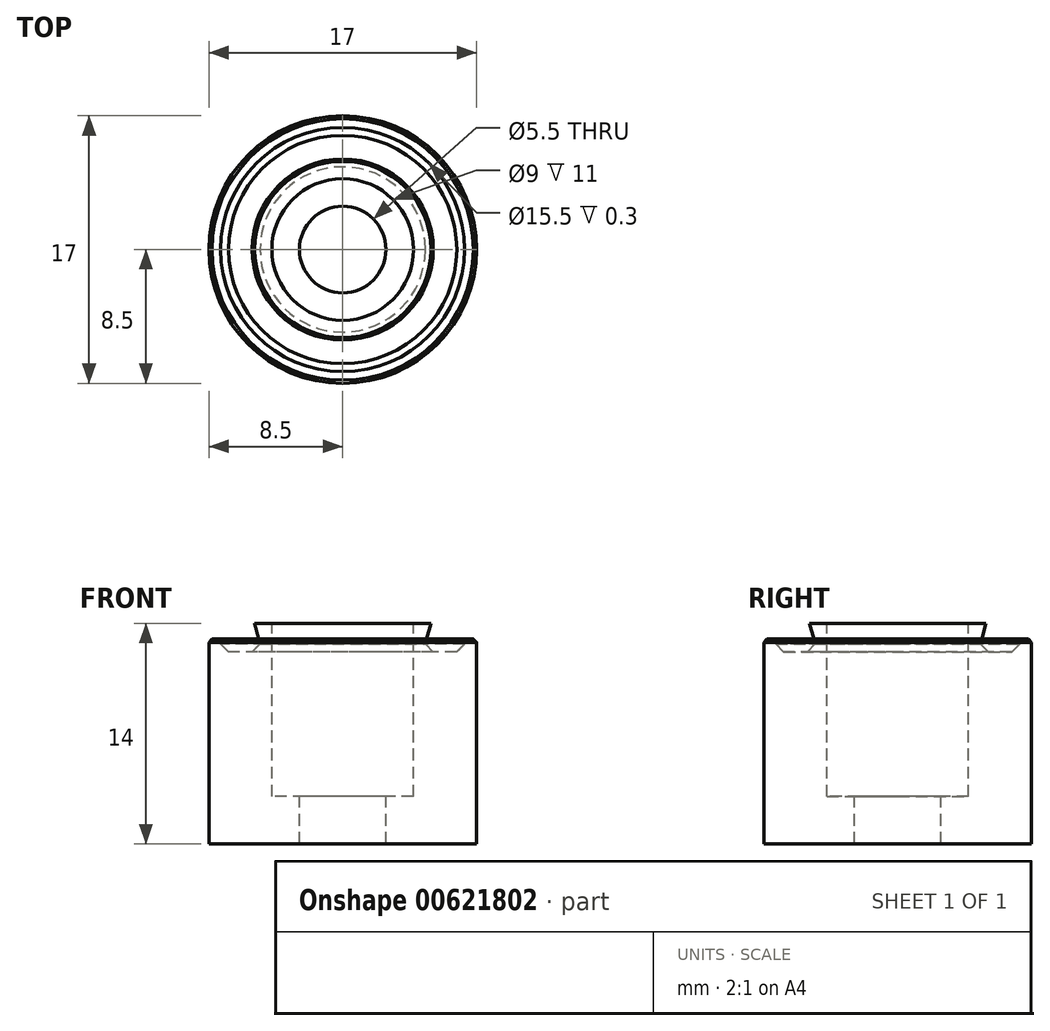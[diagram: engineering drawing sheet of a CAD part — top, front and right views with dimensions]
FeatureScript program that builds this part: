
annotation { "Feature Type Name" : "Feature", "Feature Type Description" : "" }
export const myFeature = defineFeature(function(context is Context, id is Id, definition is map)
    precondition{}
    {
        {
            var Q0;
            Q0=qCreatedBy(makeId("Top.planeOp"),FACE);
            var sketch = newSketch(context, id + "F0", { "sketchPlane" : qUnion([Q0])});
            skCircle(sketch, "E0", {"center": v(0, 0) * mm, "radius": 8.5 * mm});
            skSolve(sketch);
        }
        {
            var Q0;
            Q0 = qSketchRegion(id + "F0", true);
            extrude(context, id + "F1", {"entities" : qUnion([Q0]), "depth" : 13 * mm, "offsetDistance" : 25 * mm});
        }
        {
            var Q0;
            Q0=makeQuery(id+"F1.opExtrude","CAP_FACE",FACE,{"disambiguationData":[OSD([sQuery(id+"F0.wireOp",EDGE,"E0")])],"isStart":false});
            var sketch = newSketch(context, id + "F2", { "sketchPlane" : qUnion([Q0])});
            skCircle(sketch, "E1", {"center": v(0, 0) * mm, "radius": 2.75 * mm});
            skSolve(sketch);
        }
        {
            var Q0;
            Q0 = qSketchRegion(id + "F2", true);
            extrude(context, id + "F3", {"entities" : qUnion([Q0]), "operationType" : NewBodyOperationType.REMOVE, "endBound" : BoundingType.THROUGH_ALL, "oppositeDirection" : true, "depth" : 25 * mm, "offsetDistance" : 25 * mm});
        }
        {
            var Q0;
            Q0=makeQuery(id+"F1.opExtrude","CAP_FACE",FACE,{"disambiguationData":[OSD([sQuery(id+"F0.wireOp",EDGE,"E0")])],"isStart":false});
            var sketch = newSketch(context, id + "F4", { "sketchPlane" : qUnion([Q0])});
            skCircle(sketch, "E2", {"center": v(0, 0) * mm, "radius": 4.5 * mm});
            skSolve(sketch);
        }
        {
            var Q0;
            Q0 = qSketchRegion(id + "F4", true);
            extrude(context, id + "F5", {"entities" : qUnion([Q0]), "operationType" : NewBodyOperationType.REMOVE, "oppositeDirection" : true, "depth" : 10 * mm, "offsetDistance" : 25 * mm});
        }
        {
            var Q0;
            Q0=makeQuery(id+"F1.opExtrude","CAP_EDGE",EDGE,{"disambiguationData":[OSD([sQuery(id+"F0.wireOp",EDGE,"E0")])],"isStart":false});
            chamfer(context, id + "F6", {"entities" : qUnion([Q0]), "width" : 0.2 * mm, "tangentPropagation" : true});
        }
        {
            var Q0;
            Q0=makeQuery(id+"F1.opExtrude","CAP_FACE",FACE,{"disambiguationData":[OSD([sQuery(id+"F0.wireOp",EDGE,"E0")])],"isStart":false});
            var sketch = newSketch(context, id + "F7", { "sketchPlane" : qUnion([Q0])});
            skCircle(sketch, "E3", {"center": v(0, 0) * mm, "radius": 7.75 * mm});
            skCircle(sketch, "E4", {"center": v(0, 0) * mm, "radius": 5.25 * mm});
            skSolve(sketch);
        }
        {
            var Q0;
            Q0 = qSketchRegion(id + "F7", true);
            var Q1;
            Q1=sQuery(id+"F7.wireOp",EDGE,"E3");
            extrude(context, id + "F8", {"entities" : qUnion([Q0]), "operationType" : NewBodyOperationType.REMOVE, "surfaceEntities" : qUnion([Q1]), "oppositeDirection" : true, "depth" : 0.8 * mm, "offsetDistance" : 25 * mm});
        }
        {
            var Q0;
            Q0=makeQuery(id+"F10.imprint","IMPRINT",FACE,{"disambiguationData":[TD([[makeQuery(id+"F10.imprint","IMPRINT",EDGE,{"derivedFrom":sQuery(id+"F10.wireOp",EDGE,"35f739f2-e14d-42ed-acb1-5e8376def7af.0")}),-1.0]])]});
            var Q1;
            Q1=makeQuery(id+"F8.boolean.opBoolean","SPLIT",FACE,{"disambiguationData":[TD([makeQuery(id+"F5.boolean.opBoolean","COPY",FACE,{"derivedFrom":makeQuery(id+"F5.opExtrude","SWEPT_FACE",FACE,{"disambiguationData":[OSD([sQuery(id+"F4.wireOp",EDGE,"E2")])]})})])],"derivedFrom":makeQuery(id+"F1.opExtrude","CAP_FACE",FACE,{"disambiguationData":[OSD([sQuery(id+"F0.wireOp",EDGE,"E0")])],"isStart":false})});
            extrude(context, id + "F9", {"entities" : qUnion([Q0, Q1]), "operationType" : NewBodyOperationType.ADD, "depth" : 1 * mm, "offsetDistance" : 25 * mm});
        }
        {
            var Q0;
            Q0=makeQuery(id+"F9.opExtrude","CAP_FACE",FACE,{"disambiguationData":[OSD([sQuery(id+"F0.wireOp",EDGE,"E0")])],"isStart":false});
            var sketch = newSketch(context, id + "F10", { "sketchPlane" : qUnion([Q0])});
            skCircle(sketch, "E5", {"center": v(0, 0) * mm, "radius": 5.6 * mm});
            skCircle(sketch, "E6.0", {"center": v(0, 0) * mm, "radius": 4.5 * mm});
            skSolve(sketch);
        }
        {
            var Q0;
            Q0 = qSketchRegion(id + "F10", true);
            extrude(context, id + "F11", {"entities" : qUnion([Q0]), "operationType" : NewBodyOperationType.ADD, "oppositeDirection" : true, "depth" : 1.5 * mm, "offsetDistance" : 25 * mm, "hasDraft" : true, "draftAngle" : 15 * degree, "draftPullDirection" : true});
        }
        {
            var Q0;
            Q0=makeQuery(id+"F8.boolean.opBoolean","COPY",EDGE,{"derivedFrom":makeQuery(id+"F8.opExtrude","CAP_EDGE",EDGE,{"disambiguationData":[OSD([sQuery(id+"F7.wireOp",EDGE,"E3")])],"isStart":false})});
            var Q1;
            Q1=makeQuery(id+"F8.boolean.opBoolean","COPY",EDGE,{"derivedFrom":makeQuery(id+"F8.opExtrude","CAP_EDGE",EDGE,{"disambiguationData":[OSD([sQuery(id+"F7.wireOp",EDGE,"E4")])],"isStart":false})});
            chamfer(context, id + "F12", {"entities" : qUnion([Q0, Q1]), "width" : .5 * mm, "tangentPropagation" : true});
        }
    });
